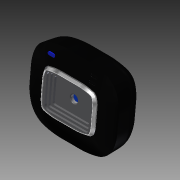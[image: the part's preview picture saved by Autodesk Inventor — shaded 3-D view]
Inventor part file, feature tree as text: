
AUTODESK INVENTOR PART (.ipt)
format: ipt  version: 2016 SP1 (Build 200210100, 210)  size: 1,805,312 bytes
history: native  units: mm
features: sketch x18, extrude x13, plane x12, fillet x6, sweep x5, other x5, thicken_offset x4, mirror x3, projected_geometry x3
ambient origin geometry x8: Origin, YZ Plane, XZ Plane, XY Plane, X Axis, Y Axis, Z Axis, Center Point
bodies: Body1 (feature_tree), Body2 (feature_tree), Body3 (feature_tree), Body4 (feature_tree), Body5 (feature_tree)
feature tree (69):
  sketch  "Sketch1"  dims[d0=109.0mm d1=44.5mm d189=90.0deg]
  plane  "Work Plane8"
  plane  "Work Plane7"
  sketch  "Sketch3"  dims[d190=3.0mm d193=0.0mm d194=0.0mm]
  plane  "Work Plane6"
  plane  "Work Plane1"
  sketch  "Sketch5"  dims[d201=0.5mm d202=0.5mm]
  plane  "Work Plane2"
  sketch  "Sketch6"  dims[d204=0.5mm d205=0.2mm]
  plane  "Work Plane5"
  sketch  "Sketch8"  dims[d210=15.0mm d211=-0.872665mm d212=10.0mm]
  mirror  "Mirror1"
  thicken_offset  "Thicken1"
  thicken_offset  "Thicken2"
  mirror  "Mirror3"
  thicken_offset  "Thicken4"
  thicken_offset  "Thicken5"
  extrude  "Extrusion6"  Depth=44.5mm
  fillet  "Fillet1"  [1 undecoded]
  sketch  "Sketch12"  dims[d220=5.0mm d221=0.0mm d224=-1.0mm]
  plane  "Work Plane9"
  sweep  "Sweep1"
  mirror  "Mirror4"
  plane  "Work Plane11"
  extrude  "Extrusion9"  Depth=0.5mm
  plane  "Work Plane13"
  extrude  "Extrusion10"  Depth=0.2mm
  plane  "Work Plane14"
  extrude  "Extrusion11"  Depth=10.0mm
  plane  "Work Plane15"
  extrude  "Extrusion12"  [1 undecoded]
  plane  "Work Plane16"
  sketch  "Sketch20"  dims[d242=1.0mm d243=1.0mm]
  extrude  "Extrusion13"  [1 undecoded]
  extrude  "Extrusion15"  Depth=11.0mm
  sketch  "Sketch21"  dims[d245=1.0mm d246=1.0mm d247=1.0mm d248=0.0mm d249=0.0mm]
  extrude  "Extrusion16"  Depth=8.0mm
  fillet  "Fillet2"  Radius=2.0mm
  sketch  "Sketch22"  dims[d250=3.0mm d251=0.0mm d255=2.75mm d256=0.0mm]
  extrude  "Extrusion17"  [1 undecoded]
  extrude  "Extrusion18"  Depth=6.0mm TaperAngle=0.0deg
  fillet  "Fillet3"  [1 undecoded]
  extrude  "Extrusion19"  Depth=1.0mm
  fillet  "Fillet4"  Radius=1.0mm
  extrude  "Extrusion20"  Depth=1.0mm
  extrude  "Extrusion21"  Depth=1.0mm
  fillet  "Fillet5"  Radius=1.0mm
  fillet  "Fillet6"  [1 undecoded]
  other  "Image4"
  other  "Srf3"
  other  "Srf4"
  other  "Srf7"
  other  "Srf8"
  sketch  "Sketch11"  dims[d213=0.0mm d214=0.0mm d219=-0.5mm]
  sketch  "Sketch13"  dims[d225=22.0mm d226=11.0mm]
  sketch  "Sketch15"  dims[d227=16.0mm d228=8.0mm d229=2.0mm]
  projected_geometry  "Projected Loop7"
  sketch  "Sketch17"  dims[d230=1.0mm d231=0.0mm d232=-1.0mm]
  sketch  "Sketch18"  dims[d233=1.0mm d234=6.0mm d235=0.0mm d236=-1.0mm]
  sketch  "Sketch19"  dims[d237=1.0mm d240=1.0mm d241=1.0mm]
  sketch  "Sketch23"  dims[d257=2.0mm d258=0.0mm d259=0.1mm]
  sketch  "Sketch24"  dims[d260=2.1mm d261=0.0mm d262=2.75mm d263=0.0mm]
  sketch  "Sketch25"  dims[d264=0.1mm d265=1.5mm d266=0.0mm d267=0.5mm d268=10.0mm d269=0.0mm d270=5.0mm d271=5.0mm d272=0.0mm d273=3.0mm d274=0.5mm d275=15.0mm d276=14.0mm]
  projected_geometry  "Projected Loop10"
  sweep  "SweepSrf1"
  sweep  "SweepSrf2"
  sweep  "SweepSrf5"
  sweep  "SweepSrf6"
  projected_geometry  "Project Cut Edges1"
note: 6 required parameter values undecoded (feature->parameter linkage not recoverable at this tier; creation-order binding heuristic only, values carry confidence <= 0.55)
